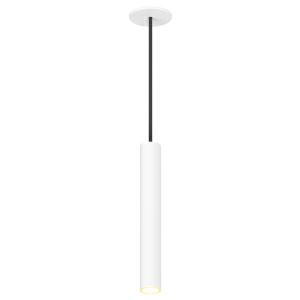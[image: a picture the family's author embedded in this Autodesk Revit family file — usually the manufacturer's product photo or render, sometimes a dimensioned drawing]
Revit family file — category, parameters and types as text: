
# Revit family: hangover_410-7840
name_source: partatom
category: Lighting Fixtures
units: mm (PartAtom-declared; Revit-internal decimal feet)

## family parameters
Cut with Voids When Loaded = No
Host = Face
Light Source = No
Part Type = Normal
Room Calculation Point = No
Round Connector Dimension = Use Diameter
Shared = No

## types (1)
- 410-7840-H27-K40-L00 (1 x LED, 969.41 lm, 9.8 W, 2700K)
    Apparent Load = 10 VA
    CIE Flux Codes = 98 100 100 100 72
    Color Rendering = 1A/90…99
    Color Temperature = 2700K
    Default Elevation = 1800 mm
    Description = HANGOVER
    Height = 300 mm
    Lamp = 1 x LED
    Lamp Light Flux = 969.41 lm
    Lamp Power = 9.8 W
    Lamp count = 1
    Length = 40 mm
    Luminous efficacy = 71 lm/W
    Manufacturer = Prolicht
    ModVariant = No
    Model = 410-7840
    Mounting Place = Ceiling
    Mounting Type = Pendant
    Number of Poles = 1
    OnlyDefault = Yes
    Power Factor = 1
    Product Name = HANGOVER
    Product group = Suspended spotlights
    ProductGroupID = 942
    Protection Class = Protection class
    Protection Degree = Degree of protection
    RLX_Detail_Level = 1
    RlxData = <blob elided: 31225 chars, md5=ffc31332>
    Socket = socket
    Standby Power = 0 W
    System Light Flux = 694 lm
    System Power = 10 W
    Type Comments = LED COLOUR DIR 2700 K (27),REFLECTOR 40° (40),SHINE RING ABSICHTLICH_LEER (00)
    Type Image = 410-7840.jpg
    URL = http://relux.com
    VarID = 410-7840-h27-k40-l00
    Voltage = 0 V
    Weight = 0.00 kg
    Width = 0 mm  [stored 0 ft]

note: [stored X ft] marks values corroborated as IEEE doubles in the binary element streams (Revit-internal decimal feet)

## geometry (parser evidence)
native form markers: Blend x4, Sweep x8
no freeform markers — native parametric forms only
